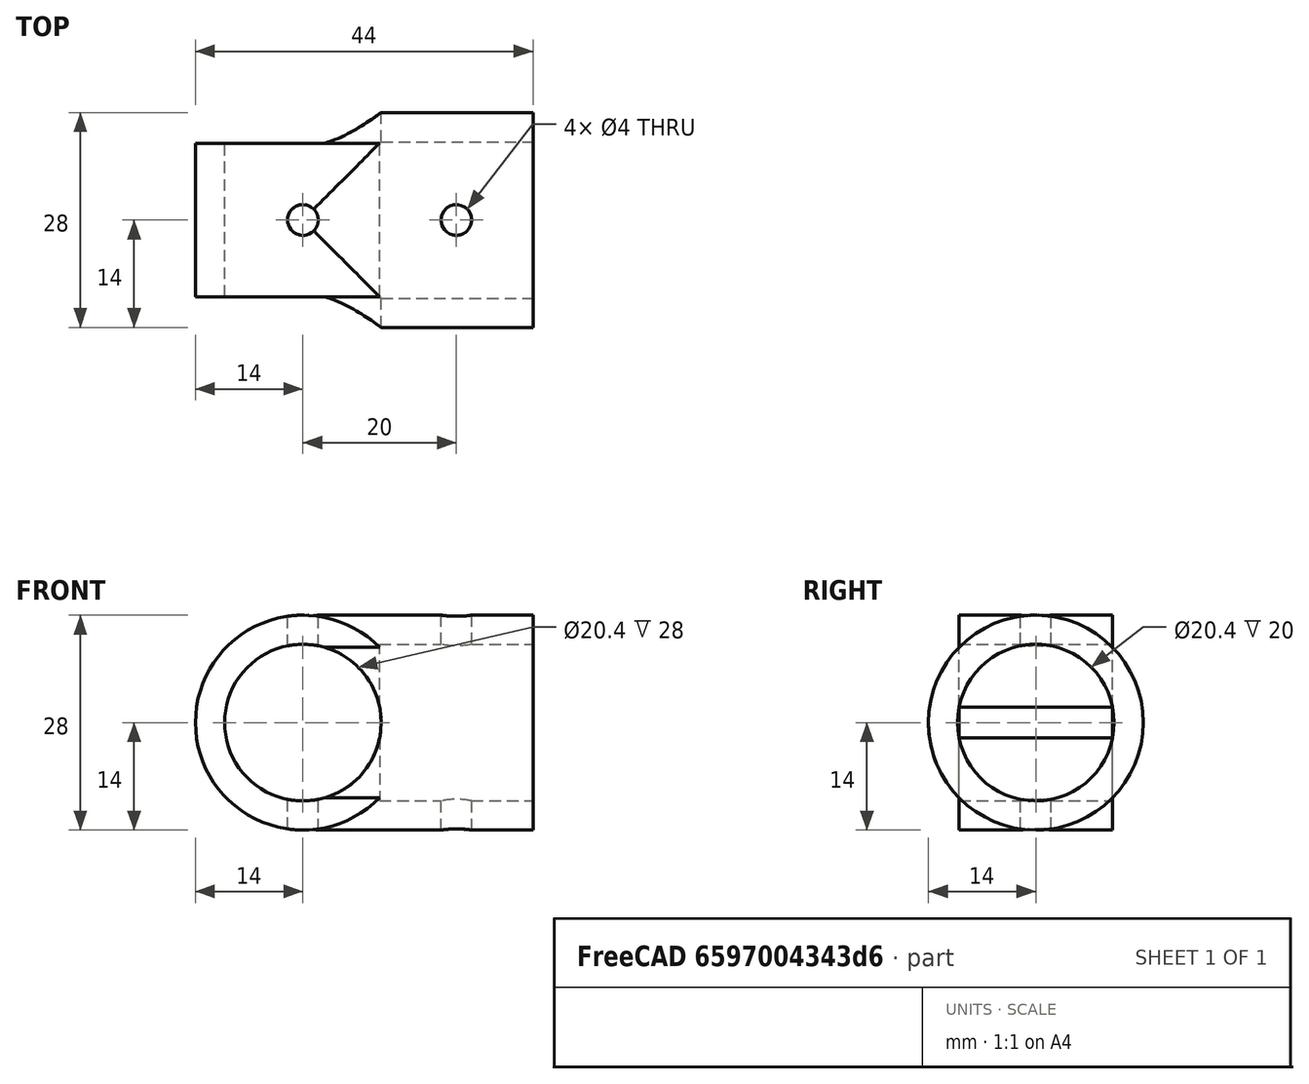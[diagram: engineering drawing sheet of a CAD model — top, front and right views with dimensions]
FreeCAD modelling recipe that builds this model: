
FCSTD DOCUMENT  (FreeCAD 0.17R13522 (Git))
Label: connector-t
License: All rights reserved
LicenseURL: http://en.wikipedia.org/wiki/All_rights_reserved
objects: Part::Cylinder×6, Part::MultiFuse×2, Part::Cut×1
note: 9 computed .brp shape members not serialized (recipe doc carries the construction recipe); baked Part::Feature solids carry a one-line shape summary decoded from their .brp

FEATURE [Part::Cylinder] Cylinder
  Angle = 360
  AttacherType = Attacher::AttachEngine3D
  Height = 30
  Placement = pos=(0,-15,0) rot=(-1,0,0;1.5708rad)
  Radius = 10.2
FEATURE [Part::Cylinder] Cylinder001
  Angle = 360
  AttacherType = Attacher::AttachEngine3D
  Height = 20
  Placement = pos=(10,0,0) rot=(0.57735,-0.57735,0.57735;4.18879rad)
  Radius = 10.2
FEATURE [Part::Cylinder] Cylinder002
  Angle = 360
  AttacherType = Attacher::AttachEngine3D
  Height = 30
  Placement = pos=(0,0,-15) rot=(0,0,1;0rad)
  Radius = 2
FEATURE [Part::Cylinder] Cylinder003
  Angle = 360
  AttacherType = Attacher::AttachEngine3D
  Height = 30
  Placement = pos=(20,0,-15) rot=(0,0,1;0rad)
  Radius = 2
FEATURE [Part::MultiFuse] Fusion  label="Negative Fusion"
  Shapes = -> [Cylinder,Cylinder001,Cylinder002,Cylinder003]
FEATURE [Part::Cylinder] Cylinder004
  Angle = 360
  AttacherType = Attacher::AttachEngine3D
  Height = 30
  Placement = pos=(0,0,0) rot=(0.57735,-0.57735,0.57735;4.18879rad)
  Radius = 14
FEATURE [Part::Cylinder] Cylinder005
  Angle = 360
  AttacherType = Attacher::AttachEngine3D
  Height = 20
  Placement = pos=(0,-10,0) rot=(-1,0,0;1.5708rad)
  Radius = 14
FEATURE [Part::MultiFuse] Fusion001
  Shapes = -> [Cylinder005,Cylinder004]
FEATURE [Part::Cut] Cut
  Base = -> Fusion001
  Tool = -> Fusion
